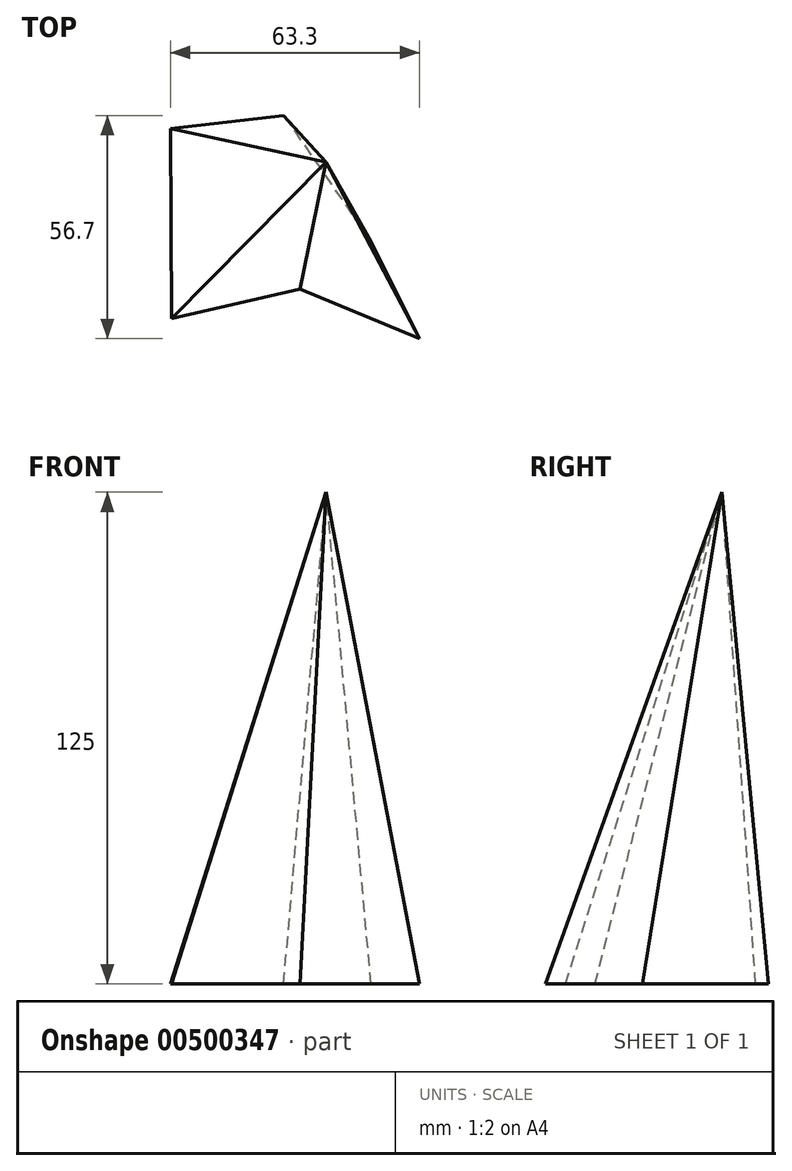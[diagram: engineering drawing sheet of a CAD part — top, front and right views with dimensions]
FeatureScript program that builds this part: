
annotation { "Feature Type Name" : "Feature", "Feature Type Description" : "" }
export const myFeature = defineFeature(function(context is Context, id is Id, definition is map)
    precondition{}
    {
        {
            var Q0;
            Q0=qCreatedBy(makeId("Top.planeOp"),FACE);
            var sketch = newSketch(context, id + "F0", { "sketchPlane" : qUnion([Q0])});
            skLineSegment(sketch, "E0", {"start": v(-39.6, 8.55) * mm, "end": v(-39.3, -39.75) * mm});
            skLineSegment(sketch, "E1", {"start": v(-39.6, 8.55) * mm, "end": v(-10.8, 11.85) * mm});
            skLineSegment(sketch, "E2", {"start": v(-10.8, 11.85) * mm, "end": v(11.4, -20.25) * mm});
            skLineSegment(sketch, "E3", {"start": v(11.4, -20.25) * mm, "end": v(23.7, -44.85) * mm});
            skLineSegment(sketch, "E4", {"start": v(23.7, -44.85) * mm, "end": v(-6.6, -32.25) * mm});
            skLineSegment(sketch, "E5", {"start": v(-6.6, -32.25) * mm, "end": v(-39.3, -39.75) * mm});
            skSolve(sketch);
        }
        {
            var Q0;
            Q0=qCreatedBy(makeId("Top.planeOp"),FACE);
            cPlane(context, id + "F1", {"entities" : qUnion([Q0]), "cplaneType" : CPlaneType.OFFSET, "offset" : 125 * mm, "width" : 150 * mm, "height" : 150 * mm});
        }
        {
            var Q0;
            Q0=qCreatedBy(id+"F1.planeOp",FACE);
            var sketch = newSketch(context, id + "F2", { "sketchPlane" : qUnion([Q0])});
            skPoint(sketch, "E6", {"position": v(0, 0) * mm});
            skSolve(sketch);
        }
        {
            var Q0;
            Q0=makeQuery(id+"F0.imprint","IMPRINT",FACE,{"disambiguationData":[TD([[makeQuery(id+"F0.imprint","IMPRINT",EDGE,{"derivedFrom":sQuery(id+"F0.wireOp",EDGE,"E0")}),1.0]])]});
            var Q1;
            Q1=sQuery(id+"F2.wireOp",VERTEX,"E6");
            loft(context, id + "F3", {"sheetProfilesArray" : [{ "sheetProfileEntities" : qUnion([Q0]) }, { "sheetProfileEntities" : qUnion([Q1]) }]});
        }
    });
